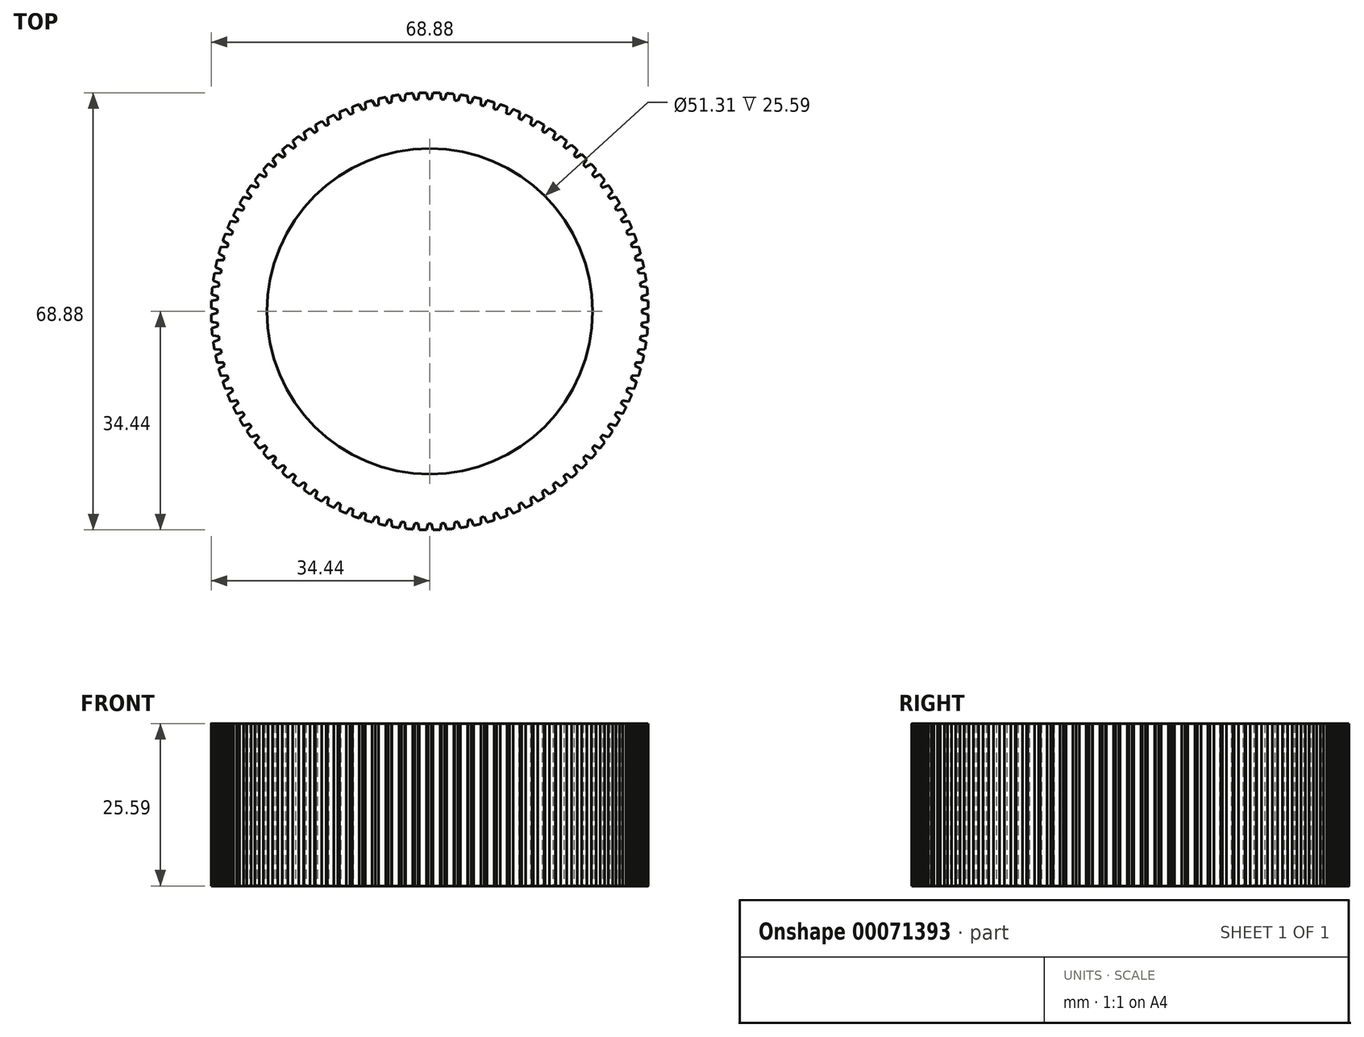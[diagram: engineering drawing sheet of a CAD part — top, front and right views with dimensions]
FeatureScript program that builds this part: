
annotation { "Feature Type Name" : "Feature", "Feature Type Description" : "" }
export const myFeature = defineFeature(function(context is Context, id is Id, definition is map)
    precondition{}
    {
        {
            var Q0;
            Q0=qCreatedBy(makeId("Top.planeOp"),FACE);
            var sketch = newSketch(context, id + "F0", { "sketchPlane" : qUnion([Q0])});
            skArc(sketch, "E0", {"start": v(-0.5, 34.44) * mm, "mid": v(-1.08, 34.43) * mm, "end": v(-1.66, 34.4) * mm});
            skCircle(sketch, "E1", {"center": v(0, 0) * mm, "radius": 25.66 * mm});
            skLineSegment(sketch, "E2", {"start": v(-0.5, 34.44) * mm, "end": v(-0.25, 33.46) * mm});
            skLineSegment(sketch, "E3", {"start": v(0.25, 33.46) * mm, "end": v(0.5, 34.44) * mm});
            skLineSegment(sketch, "E4.1.0", {"start": v(-1.85, 33.41) * mm, "end": v(-1.66, 34.4) * mm});
            skLineSegment(sketch, "E4.1.1", {"start": v(-2.66, 34.34) * mm, "end": v(-2.35, 33.38) * mm});
            skLineSegment(sketch, "E4.2.0", {"start": v(-3.95, 33.23) * mm, "end": v(-3.82, 34.23) * mm});
            skLineSegment(sketch, "E4.2.1", {"start": v(-4.81, 34.1) * mm, "end": v(-4.44, 33.17) * mm});
            skLineSegment(sketch, "E4.3.0", {"start": v(-6.02, 32.92) * mm, "end": v(-5.96, 33.93) * mm});
            skLineSegment(sketch, "E4.3.1", {"start": v(-6.94, 33.74) * mm, "end": v(-6.52, 32.82) * mm});
            skLineSegment(sketch, "E4.4.0", {"start": v(-8.08, 32.47) * mm, "end": v(-8.08, 33.48) * mm});
            skLineSegment(sketch, "E4.4.1", {"start": v(-9.05, 33.23) * mm, "end": v(-8.56, 32.35) * mm});
            skLineSegment(sketch, "E4.5.0", {"start": v(-10.1, 31.9) * mm, "end": v(-10.17, 32.91) * mm});
            skLineSegment(sketch, "E4.5.1", {"start": v(-11.12, 32.6) * mm, "end": v(-10.58, 31.75) * mm});
            skLineSegment(sketch, "E4.6.0", {"start": v(-12.09, 31.2) * mm, "end": v(-12.21, 32.2) * mm});
            skLineSegment(sketch, "E4.6.1", {"start": v(-13.14, 31.84) * mm, "end": v(-12.55, 31.02) * mm});
            skLineSegment(sketch, "E4.7.0", {"start": v(-14.02, 30.39) * mm, "end": v(-14.21, 31.38) * mm});
            skLineSegment(sketch, "E4.7.1", {"start": v(-15.12, 30.95) * mm, "end": v(-14.47, 30.17) * mm});
            skLineSegment(sketch, "E4.8.0", {"start": v(-15.9, 29.44) * mm, "end": v(-16.15, 30.42) * mm});
            skLineSegment(sketch, "E4.8.1", {"start": v(-17.03, 29.94) * mm, "end": v(-16.34, 29.2) * mm});
            skLineSegment(sketch, "E4.9.0", {"start": v(-17.72, 28.39) * mm, "end": v(-18.03, 29.35) * mm});
            skLineSegment(sketch, "E4.9.1", {"start": v(-18.88, 28.81) * mm, "end": v(-18.14, 28.12) * mm});
            skLineSegment(sketch, "E4.10.0", {"start": v(-19.47, 27.22) * mm, "end": v(-19.84, 28.16) * mm});
            skLineSegment(sketch, "E4.10.1", {"start": v(-20.65, 27.57) * mm, "end": v(-19.87, 26.93) * mm});
            skLineSegment(sketch, "E4.11.0", {"start": v(-21.14, 25.94) * mm, "end": v(-21.57, 26.86) * mm});
            skLineSegment(sketch, "E4.11.1", {"start": v(-22.34, 26.22) * mm, "end": v(-21.52, 25.62) * mm});
            skLineSegment(sketch, "E4.12.0", {"start": v(-22.73, 24.56) * mm, "end": v(-23.21, 25.45) * mm});
            skLineSegment(sketch, "E4.12.1", {"start": v(-23.94, 24.76) * mm, "end": v(-23.09, 24.22) * mm});
            skLineSegment(sketch, "E4.13.0", {"start": v(-24.22, 23.09) * mm, "end": v(-24.76, 23.94) * mm});
            skLineSegment(sketch, "E4.13.1", {"start": v(-25.45, 23.21) * mm, "end": v(-24.56, 22.73) * mm});
            skLineSegment(sketch, "E4.14.0", {"start": v(-25.62, 21.52) * mm, "end": v(-26.22, 22.34) * mm});
            skLineSegment(sketch, "E4.14.1", {"start": v(-26.86, 21.57) * mm, "end": v(-25.94, 21.14) * mm});
            skLineSegment(sketch, "E4.15.0", {"start": v(-26.93, 19.87) * mm, "end": v(-27.57, 20.65) * mm});
            skLineSegment(sketch, "E4.15.1", {"start": v(-28.16, 19.84) * mm, "end": v(-27.22, 19.47) * mm});
            skLineSegment(sketch, "E4.16.0", {"start": v(-28.12, 18.14) * mm, "end": v(-28.81, 18.88) * mm});
            skLineSegment(sketch, "E4.16.1", {"start": v(-29.35, 18.03) * mm, "end": v(-28.39, 17.72) * mm});
            skLineSegment(sketch, "E4.17.0", {"start": v(-29.2, 16.34) * mm, "end": v(-29.94, 17.03) * mm});
            skLineSegment(sketch, "E4.17.1", {"start": v(-30.42, 16.15) * mm, "end": v(-29.44, 15.9) * mm});
            skLineSegment(sketch, "E4.18.0", {"start": v(-30.17, 14.47) * mm, "end": v(-30.95, 15.12) * mm});
            skLineSegment(sketch, "E4.18.1", {"start": v(-31.38, 14.21) * mm, "end": v(-30.39, 14.02) * mm});
            skLineSegment(sketch, "E4.19.0", {"start": v(-31.02, 12.55) * mm, "end": v(-31.84, 13.14) * mm});
            skLineSegment(sketch, "E4.19.1", {"start": v(-32.2, 12.21) * mm, "end": v(-31.2, 12.09) * mm});
            skLineSegment(sketch, "E4.20.0", {"start": v(-31.75, 10.58) * mm, "end": v(-32.6, 11.12) * mm});
            skLineSegment(sketch, "E4.20.1", {"start": v(-32.91, 10.17) * mm, "end": v(-31.9, 10.1) * mm});
            skLineSegment(sketch, "E4.21.0", {"start": v(-32.35, 8.56) * mm, "end": v(-33.23, 9.05) * mm});
            skLineSegment(sketch, "E4.21.1", {"start": v(-33.48, 8.08) * mm, "end": v(-32.47, 8.08) * mm});
            skLineSegment(sketch, "E4.22.0", {"start": v(-32.82, 6.52) * mm, "end": v(-33.74, 6.94) * mm});
            skLineSegment(sketch, "E4.22.1", {"start": v(-33.93, 5.96) * mm, "end": v(-32.92, 6.02) * mm});
            skLineSegment(sketch, "E4.23.0", {"start": v(-33.17, 4.44) * mm, "end": v(-34.1, 4.81) * mm});
            skLineSegment(sketch, "E4.23.1", {"start": v(-34.23, 3.82) * mm, "end": v(-33.23, 3.95) * mm});
            skLineSegment(sketch, "E4.24.0", {"start": v(-33.38, 2.35) * mm, "end": v(-34.34, 2.66) * mm});
            skLineSegment(sketch, "E4.24.1", {"start": v(-34.4, 1.66) * mm, "end": v(-33.41, 1.85) * mm});
            skLineSegment(sketch, "E4.25.0", {"start": v(-33.46, 0.25) * mm, "end": v(-34.44, 0.5) * mm});
            skLineSegment(sketch, "E4.25.1", {"start": v(-34.44, -0.5) * mm, "end": v(-33.46, -0.25) * mm});
            skLineSegment(sketch, "E4.26.0", {"start": v(-33.41, -1.85) * mm, "end": v(-34.4, -1.66) * mm});
            skLineSegment(sketch, "E4.26.1", {"start": v(-34.34, -2.66) * mm, "end": v(-33.38, -2.35) * mm});
            skLineSegment(sketch, "E4.27.0", {"start": v(-33.23, -3.95) * mm, "end": v(-34.23, -3.82) * mm});
            skLineSegment(sketch, "E4.27.1", {"start": v(-34.1, -4.81) * mm, "end": v(-33.17, -4.44) * mm});
            skLineSegment(sketch, "E4.28.0", {"start": v(-32.92, -6.02) * mm, "end": v(-33.93, -5.96) * mm});
            skLineSegment(sketch, "E4.28.1", {"start": v(-33.74, -6.94) * mm, "end": v(-32.82, -6.52) * mm});
            skLineSegment(sketch, "E4.29.0", {"start": v(-32.47, -8.08) * mm, "end": v(-33.48, -8.08) * mm});
            skLineSegment(sketch, "E4.29.1", {"start": v(-33.23, -9.05) * mm, "end": v(-32.35, -8.56) * mm});
            skLineSegment(sketch, "E4.30.0", {"start": v(-31.9, -10.1) * mm, "end": v(-32.91, -10.17) * mm});
            skLineSegment(sketch, "E4.30.1", {"start": v(-32.6, -11.12) * mm, "end": v(-31.75, -10.58) * mm});
            skLineSegment(sketch, "E4.31.0", {"start": v(-31.2, -12.09) * mm, "end": v(-32.2, -12.21) * mm});
            skLineSegment(sketch, "E4.31.1", {"start": v(-31.84, -13.14) * mm, "end": v(-31.02, -12.55) * mm});
            skLineSegment(sketch, "E4.32.0", {"start": v(-30.39, -14.02) * mm, "end": v(-31.38, -14.21) * mm});
            skLineSegment(sketch, "E4.32.1", {"start": v(-30.95, -15.12) * mm, "end": v(-30.17, -14.47) * mm});
            skLineSegment(sketch, "E4.33.0", {"start": v(-29.44, -15.9) * mm, "end": v(-30.42, -16.15) * mm});
            skLineSegment(sketch, "E4.33.1", {"start": v(-29.94, -17.03) * mm, "end": v(-29.2, -16.34) * mm});
            skLineSegment(sketch, "E4.34.0", {"start": v(-28.39, -17.72) * mm, "end": v(-29.35, -18.03) * mm});
            skLineSegment(sketch, "E4.34.1", {"start": v(-28.81, -18.88) * mm, "end": v(-28.12, -18.14) * mm});
            skLineSegment(sketch, "E4.35.0", {"start": v(-27.22, -19.47) * mm, "end": v(-28.16, -19.84) * mm});
            skLineSegment(sketch, "E4.35.1", {"start": v(-27.57, -20.65) * mm, "end": v(-26.93, -19.87) * mm});
            skLineSegment(sketch, "E4.36.0", {"start": v(-25.94, -21.14) * mm, "end": v(-26.86, -21.57) * mm});
            skLineSegment(sketch, "E4.36.1", {"start": v(-26.22, -22.34) * mm, "end": v(-25.62, -21.52) * mm});
            skLineSegment(sketch, "E4.37.0", {"start": v(-24.56, -22.73) * mm, "end": v(-25.45, -23.21) * mm});
            skLineSegment(sketch, "E4.37.1", {"start": v(-24.76, -23.94) * mm, "end": v(-24.22, -23.09) * mm});
            skLineSegment(sketch, "E4.38.0", {"start": v(-23.09, -24.22) * mm, "end": v(-23.94, -24.76) * mm});
            skLineSegment(sketch, "E4.38.1", {"start": v(-23.21, -25.45) * mm, "end": v(-22.73, -24.56) * mm});
            skLineSegment(sketch, "E4.39.0", {"start": v(-21.52, -25.62) * mm, "end": v(-22.34, -26.22) * mm});
            skLineSegment(sketch, "E4.39.1", {"start": v(-21.57, -26.86) * mm, "end": v(-21.14, -25.94) * mm});
            skLineSegment(sketch, "E4.40.0", {"start": v(-19.87, -26.93) * mm, "end": v(-20.65, -27.57) * mm});
            skLineSegment(sketch, "E4.40.1", {"start": v(-19.84, -28.16) * mm, "end": v(-19.47, -27.22) * mm});
            skLineSegment(sketch, "E4.41.0", {"start": v(-18.14, -28.12) * mm, "end": v(-18.88, -28.81) * mm});
            skLineSegment(sketch, "E4.41.1", {"start": v(-18.03, -29.35) * mm, "end": v(-17.72, -28.39) * mm});
            skLineSegment(sketch, "E4.42.0", {"start": v(-16.34, -29.2) * mm, "end": v(-17.03, -29.94) * mm});
            skLineSegment(sketch, "E4.42.1", {"start": v(-16.15, -30.42) * mm, "end": v(-15.9, -29.44) * mm});
            skLineSegment(sketch, "E4.43.0", {"start": v(-14.47, -30.17) * mm, "end": v(-15.12, -30.95) * mm});
            skLineSegment(sketch, "E4.43.1", {"start": v(-14.21, -31.38) * mm, "end": v(-14.02, -30.39) * mm});
            skLineSegment(sketch, "E4.44.0", {"start": v(-12.55, -31.02) * mm, "end": v(-13.14, -31.84) * mm});
            skLineSegment(sketch, "E4.44.1", {"start": v(-12.21, -32.2) * mm, "end": v(-12.09, -31.2) * mm});
            skLineSegment(sketch, "E4.45.0", {"start": v(-10.58, -31.75) * mm, "end": v(-11.12, -32.6) * mm});
            skLineSegment(sketch, "E4.45.1", {"start": v(-10.17, -32.91) * mm, "end": v(-10.1, -31.9) * mm});
            skLineSegment(sketch, "E4.46.0", {"start": v(-8.56, -32.35) * mm, "end": v(-9.05, -33.23) * mm});
            skLineSegment(sketch, "E4.46.1", {"start": v(-8.08, -33.48) * mm, "end": v(-8.08, -32.47) * mm});
            skLineSegment(sketch, "E4.47.0", {"start": v(-6.52, -32.82) * mm, "end": v(-6.94, -33.74) * mm});
            skLineSegment(sketch, "E4.47.1", {"start": v(-5.96, -33.93) * mm, "end": v(-6.02, -32.92) * mm});
            skLineSegment(sketch, "E4.48.0", {"start": v(-4.44, -33.17) * mm, "end": v(-4.81, -34.1) * mm});
            skLineSegment(sketch, "E4.48.1", {"start": v(-3.82, -34.23) * mm, "end": v(-3.95, -33.23) * mm});
            skLineSegment(sketch, "E4.49.0", {"start": v(-2.35, -33.38) * mm, "end": v(-2.66, -34.34) * mm});
            skLineSegment(sketch, "E4.49.1", {"start": v(-1.66, -34.4) * mm, "end": v(-1.85, -33.41) * mm});
            skLineSegment(sketch, "E4.50.0", {"start": v(-0.25, -33.46) * mm, "end": v(-0.5, -34.44) * mm});
            skLineSegment(sketch, "E4.50.1", {"start": v(0.5, -34.44) * mm, "end": v(0.25, -33.46) * mm});
            skLineSegment(sketch, "E4.51.0", {"start": v(1.85, -33.41) * mm, "end": v(1.66, -34.4) * mm});
            skLineSegment(sketch, "E4.51.1", {"start": v(2.66, -34.34) * mm, "end": v(2.35, -33.38) * mm});
            skLineSegment(sketch, "E4.52.0", {"start": v(3.95, -33.23) * mm, "end": v(3.82, -34.23) * mm});
            skLineSegment(sketch, "E4.52.1", {"start": v(4.81, -34.1) * mm, "end": v(4.44, -33.17) * mm});
            skLineSegment(sketch, "E4.53.0", {"start": v(6.02, -32.92) * mm, "end": v(5.96, -33.93) * mm});
            skLineSegment(sketch, "E4.53.1", {"start": v(6.94, -33.74) * mm, "end": v(6.52, -32.82) * mm});
            skLineSegment(sketch, "E4.54.0", {"start": v(8.08, -32.47) * mm, "end": v(8.08, -33.48) * mm});
            skLineSegment(sketch, "E4.54.1", {"start": v(9.05, -33.23) * mm, "end": v(8.56, -32.35) * mm});
            skLineSegment(sketch, "E4.55.0", {"start": v(10.1, -31.9) * mm, "end": v(10.17, -32.91) * mm});
            skLineSegment(sketch, "E4.55.1", {"start": v(11.12, -32.6) * mm, "end": v(10.58, -31.75) * mm});
            skLineSegment(sketch, "E4.56.0", {"start": v(12.09, -31.2) * mm, "end": v(12.21, -32.2) * mm});
            skLineSegment(sketch, "E4.56.1", {"start": v(13.14, -31.84) * mm, "end": v(12.55, -31.02) * mm});
            skLineSegment(sketch, "E4.57.0", {"start": v(14.02, -30.39) * mm, "end": v(14.21, -31.38) * mm});
            skLineSegment(sketch, "E4.57.1", {"start": v(15.12, -30.95) * mm, "end": v(14.47, -30.17) * mm});
            skLineSegment(sketch, "E4.58.0", {"start": v(15.9, -29.44) * mm, "end": v(16.15, -30.42) * mm});
            skLineSegment(sketch, "E4.58.1", {"start": v(17.03, -29.94) * mm, "end": v(16.34, -29.2) * mm});
            skLineSegment(sketch, "E4.59.0", {"start": v(17.72, -28.39) * mm, "end": v(18.03, -29.35) * mm});
            skLineSegment(sketch, "E4.59.1", {"start": v(18.88, -28.81) * mm, "end": v(18.14, -28.12) * mm});
            skLineSegment(sketch, "E4.60.0", {"start": v(19.47, -27.22) * mm, "end": v(19.84, -28.16) * mm});
            skLineSegment(sketch, "E4.60.1", {"start": v(20.65, -27.57) * mm, "end": v(19.87, -26.93) * mm});
            skLineSegment(sketch, "E4.61.0", {"start": v(21.14, -25.94) * mm, "end": v(21.57, -26.86) * mm});
            skLineSegment(sketch, "E4.61.1", {"start": v(22.34, -26.22) * mm, "end": v(21.52, -25.62) * mm});
            skLineSegment(sketch, "E4.62.0", {"start": v(22.73, -24.56) * mm, "end": v(23.21, -25.45) * mm});
            skLineSegment(sketch, "E4.62.1", {"start": v(23.94, -24.76) * mm, "end": v(23.09, -24.22) * mm});
            skLineSegment(sketch, "E4.63.0", {"start": v(24.22, -23.09) * mm, "end": v(24.76, -23.94) * mm});
            skLineSegment(sketch, "E4.63.1", {"start": v(25.45, -23.21) * mm, "end": v(24.56, -22.73) * mm});
            skLineSegment(sketch, "E4.64.0", {"start": v(25.62, -21.52) * mm, "end": v(26.22, -22.34) * mm});
            skLineSegment(sketch, "E4.64.1", {"start": v(26.86, -21.57) * mm, "end": v(25.94, -21.14) * mm});
            skLineSegment(sketch, "E4.65.0", {"start": v(26.93, -19.87) * mm, "end": v(27.57, -20.65) * mm});
            skLineSegment(sketch, "E4.65.1", {"start": v(28.16, -19.84) * mm, "end": v(27.22, -19.47) * mm});
            skLineSegment(sketch, "E4.66.0", {"start": v(28.12, -18.14) * mm, "end": v(28.81, -18.88) * mm});
            skLineSegment(sketch, "E4.66.1", {"start": v(29.35, -18.03) * mm, "end": v(28.39, -17.72) * mm});
            skLineSegment(sketch, "E4.67.0", {"start": v(29.2, -16.34) * mm, "end": v(29.94, -17.03) * mm});
            skLineSegment(sketch, "E4.67.1", {"start": v(30.42, -16.15) * mm, "end": v(29.44, -15.9) * mm});
            skLineSegment(sketch, "E4.68.0", {"start": v(30.17, -14.47) * mm, "end": v(30.95, -15.12) * mm});
            skLineSegment(sketch, "E4.68.1", {"start": v(31.38, -14.21) * mm, "end": v(30.39, -14.02) * mm});
            skLineSegment(sketch, "E4.69.0", {"start": v(31.02, -12.55) * mm, "end": v(31.84, -13.14) * mm});
            skLineSegment(sketch, "E4.69.1", {"start": v(32.2, -12.21) * mm, "end": v(31.2, -12.09) * mm});
            skLineSegment(sketch, "E4.70.0", {"start": v(31.75, -10.58) * mm, "end": v(32.6, -11.12) * mm});
            skLineSegment(sketch, "E4.70.1", {"start": v(32.91, -10.17) * mm, "end": v(31.9, -10.1) * mm});
            skLineSegment(sketch, "E4.71.0", {"start": v(32.35, -8.56) * mm, "end": v(33.23, -9.05) * mm});
            skLineSegment(sketch, "E4.71.1", {"start": v(33.48, -8.08) * mm, "end": v(32.47, -8.08) * mm});
            skLineSegment(sketch, "E4.72.0", {"start": v(32.82, -6.52) * mm, "end": v(33.74, -6.94) * mm});
            skLineSegment(sketch, "E4.72.1", {"start": v(33.93, -5.96) * mm, "end": v(32.92, -6.02) * mm});
            skLineSegment(sketch, "E4.73.0", {"start": v(33.17, -4.44) * mm, "end": v(34.1, -4.81) * mm});
            skLineSegment(sketch, "E4.73.1", {"start": v(34.23, -3.82) * mm, "end": v(33.23, -3.95) * mm});
            skLineSegment(sketch, "E4.74.0", {"start": v(33.38, -2.35) * mm, "end": v(34.34, -2.66) * mm});
            skLineSegment(sketch, "E4.74.1", {"start": v(34.4, -1.66) * mm, "end": v(33.41, -1.85) * mm});
            skLineSegment(sketch, "E4.75.0", {"start": v(33.46, -0.25) * mm, "end": v(34.44, -0.5) * mm});
            skLineSegment(sketch, "E4.75.1", {"start": v(34.44, 0.5) * mm, "end": v(33.46, 0.25) * mm});
            skLineSegment(sketch, "E4.76.0", {"start": v(33.41, 1.85) * mm, "end": v(34.4, 1.66) * mm});
            skLineSegment(sketch, "E4.76.1", {"start": v(34.34, 2.66) * mm, "end": v(33.38, 2.35) * mm});
            skLineSegment(sketch, "E4.77.0", {"start": v(33.23, 3.95) * mm, "end": v(34.23, 3.82) * mm});
            skLineSegment(sketch, "E4.77.1", {"start": v(34.1, 4.81) * mm, "end": v(33.17, 4.44) * mm});
            skLineSegment(sketch, "E4.78.0", {"start": v(32.92, 6.02) * mm, "end": v(33.93, 5.96) * mm});
            skLineSegment(sketch, "E4.78.1", {"start": v(33.74, 6.94) * mm, "end": v(32.82, 6.52) * mm});
            skLineSegment(sketch, "E4.79.0", {"start": v(32.47, 8.08) * mm, "end": v(33.48, 8.08) * mm});
            skLineSegment(sketch, "E4.79.1", {"start": v(33.23, 9.05) * mm, "end": v(32.35, 8.56) * mm});
            skLineSegment(sketch, "E4.80.0", {"start": v(31.9, 10.1) * mm, "end": v(32.91, 10.17) * mm});
            skLineSegment(sketch, "E4.80.1", {"start": v(32.6, 11.12) * mm, "end": v(31.75, 10.58) * mm});
            skLineSegment(sketch, "E4.81.0", {"start": v(31.2, 12.09) * mm, "end": v(32.2, 12.21) * mm});
            skLineSegment(sketch, "E4.81.1", {"start": v(31.84, 13.14) * mm, "end": v(31.02, 12.55) * mm});
            skLineSegment(sketch, "E4.82.0", {"start": v(30.39, 14.02) * mm, "end": v(31.38, 14.21) * mm});
            skLineSegment(sketch, "E4.82.1", {"start": v(30.95, 15.12) * mm, "end": v(30.17, 14.47) * mm});
            skLineSegment(sketch, "E4.83.0", {"start": v(29.44, 15.9) * mm, "end": v(30.42, 16.15) * mm});
            skLineSegment(sketch, "E4.83.1", {"start": v(29.94, 17.03) * mm, "end": v(29.2, 16.34) * mm});
            skLineSegment(sketch, "E4.84.0", {"start": v(28.39, 17.72) * mm, "end": v(29.35, 18.03) * mm});
            skLineSegment(sketch, "E4.84.1", {"start": v(28.81, 18.88) * mm, "end": v(28.12, 18.14) * mm});
            skLineSegment(sketch, "E4.85.0", {"start": v(27.22, 19.47) * mm, "end": v(28.16, 19.84) * mm});
            skLineSegment(sketch, "E4.85.1", {"start": v(27.57, 20.65) * mm, "end": v(26.93, 19.87) * mm});
            skLineSegment(sketch, "E4.86.0", {"start": v(25.94, 21.14) * mm, "end": v(26.86, 21.57) * mm});
            skLineSegment(sketch, "E4.86.1", {"start": v(26.22, 22.34) * mm, "end": v(25.62, 21.52) * mm});
            skLineSegment(sketch, "E4.87.0", {"start": v(24.56, 22.73) * mm, "end": v(25.45, 23.21) * mm});
            skLineSegment(sketch, "E4.87.1", {"start": v(24.76, 23.94) * mm, "end": v(24.22, 23.09) * mm});
            skLineSegment(sketch, "E4.88.0", {"start": v(23.09, 24.22) * mm, "end": v(23.94, 24.76) * mm});
            skLineSegment(sketch, "E4.88.1", {"start": v(23.21, 25.45) * mm, "end": v(22.73, 24.56) * mm});
            skLineSegment(sketch, "E4.89.0", {"start": v(21.52, 25.62) * mm, "end": v(22.34, 26.22) * mm});
            skLineSegment(sketch, "E4.89.1", {"start": v(21.57, 26.86) * mm, "end": v(21.14, 25.94) * mm});
            skLineSegment(sketch, "E4.90.0", {"start": v(19.87, 26.93) * mm, "end": v(20.65, 27.57) * mm});
            skLineSegment(sketch, "E4.90.1", {"start": v(19.84, 28.16) * mm, "end": v(19.47, 27.22) * mm});
            skLineSegment(sketch, "E4.91.0", {"start": v(18.14, 28.12) * mm, "end": v(18.88, 28.81) * mm});
            skLineSegment(sketch, "E4.91.1", {"start": v(18.03, 29.35) * mm, "end": v(17.72, 28.39) * mm});
            skLineSegment(sketch, "E4.92.0", {"start": v(16.34, 29.2) * mm, "end": v(17.03, 29.94) * mm});
            skLineSegment(sketch, "E4.92.1", {"start": v(16.15, 30.42) * mm, "end": v(15.9, 29.44) * mm});
            skLineSegment(sketch, "E4.93.0", {"start": v(14.47, 30.17) * mm, "end": v(15.12, 30.95) * mm});
            skLineSegment(sketch, "E4.93.1", {"start": v(14.21, 31.38) * mm, "end": v(14.02, 30.39) * mm});
            skLineSegment(sketch, "E4.94.0", {"start": v(12.55, 31.02) * mm, "end": v(13.14, 31.84) * mm});
            skLineSegment(sketch, "E4.94.1", {"start": v(12.21, 32.2) * mm, "end": v(12.09, 31.2) * mm});
            skLineSegment(sketch, "E4.95.0", {"start": v(10.58, 31.75) * mm, "end": v(11.12, 32.6) * mm});
            skLineSegment(sketch, "E4.95.1", {"start": v(10.17, 32.91) * mm, "end": v(10.1, 31.9) * mm});
            skLineSegment(sketch, "E4.96.0", {"start": v(8.56, 32.35) * mm, "end": v(9.05, 33.23) * mm});
            skLineSegment(sketch, "E4.96.1", {"start": v(8.08, 33.48) * mm, "end": v(8.08, 32.47) * mm});
            skLineSegment(sketch, "E4.97.0", {"start": v(6.52, 32.82) * mm, "end": v(6.94, 33.74) * mm});
            skLineSegment(sketch, "E4.97.1", {"start": v(5.96, 33.93) * mm, "end": v(6.02, 32.92) * mm});
            skLineSegment(sketch, "E4.98.0", {"start": v(4.44, 33.17) * mm, "end": v(4.81, 34.1) * mm});
            skLineSegment(sketch, "E4.98.1", {"start": v(3.82, 34.23) * mm, "end": v(3.95, 33.23) * mm});
            skLineSegment(sketch, "E4.99.0", {"start": v(2.35, 33.38) * mm, "end": v(2.66, 34.34) * mm});
            skLineSegment(sketch, "E4.99.1", {"start": v(1.66, 34.4) * mm, "end": v(1.85, 33.41) * mm});
            skArc(sketch, "E5.trimOffspring", {"start": v(1.66, 34.4) * mm, "mid": v(1.08, 34.43) * mm, "end": v(0.5, 34.44) * mm});
            skArc(sketch, "E6.trimOffspring", {"start": v(3.82, 34.23) * mm, "mid": v(3.24, 34.3) * mm, "end": v(2.66, 34.34) * mm});
            skArc(sketch, "E7.trimOffspring", {"start": v(5.96, 33.93) * mm, "mid": v(5.39, 34.02) * mm, "end": v(4.81, 34.1) * mm});
            skArc(sketch, "E8.trimOffspring", {"start": v(8.08, 33.48) * mm, "mid": v(7.51, 33.62) * mm, "end": v(6.94, 33.74) * mm});
            skArc(sketch, "E9.trimOffspring", {"start": v(10.17, 32.91) * mm, "mid": v(9.6, 33.08) * mm, "end": v(9.05, 33.23) * mm});
            skArc(sketch, "E10.trimOffspring", {"start": v(12.21, 32.2) * mm, "mid": v(11.67, 32.4) * mm, "end": v(11.12, 32.6) * mm});
            skArc(sketch, "E11.trimOffspring", {"start": v(14.21, 31.38) * mm, "mid": v(13.68, 31.61) * mm, "end": v(13.14, 31.84) * mm});
            skArc(sketch, "E12.trimOffspring", {"start": v(16.15, 30.42) * mm, "mid": v(15.64, 30.7) * mm, "end": v(15.12, 30.95) * mm});
            skArc(sketch, "E13.trimOffspring", {"start": v(18.03, 29.35) * mm, "mid": v(17.53, 29.65) * mm, "end": v(17.03, 29.94) * mm});
            skArc(sketch, "E14.trimOffspring", {"start": v(19.84, 28.16) * mm, "mid": v(19.36, 28.49) * mm, "end": v(18.88, 28.81) * mm});
            skArc(sketch, "E15.trimOffspring", {"start": v(21.57, 26.86) * mm, "mid": v(21.11, 27.22) * mm, "end": v(20.65, 27.57) * mm});
            skArc(sketch, "E16.trimOffspring", {"start": v(23.21, 25.45) * mm, "mid": v(22.78, 25.84) * mm, "end": v(22.34, 26.22) * mm});
            skArc(sketch, "E17.trimOffspring", {"start": v(24.76, 23.94) * mm, "mid": v(24.36, 24.36) * mm, "end": v(23.94, 24.76) * mm});
            skArc(sketch, "E18.trimOffspring", {"start": v(26.22, 22.34) * mm, "mid": v(25.84, 22.78) * mm, "end": v(25.45, 23.21) * mm});
            skArc(sketch, "E19.trimOffspring", {"start": v(27.57, 20.65) * mm, "mid": v(27.22, 21.11) * mm, "end": v(26.86, 21.57) * mm});
            skArc(sketch, "E20.trimOffspring", {"start": v(28.81, 18.88) * mm, "mid": v(28.49, 19.36) * mm, "end": v(28.16, 19.84) * mm});
            skArc(sketch, "E21.trimOffspring", {"start": v(29.94, 17.03) * mm, "mid": v(29.65, 17.53) * mm, "end": v(29.35, 18.03) * mm});
            skArc(sketch, "E22.trimOffspring", {"start": v(30.95, 15.12) * mm, "mid": v(30.7, 15.64) * mm, "end": v(30.42, 16.15) * mm});
            skArc(sketch, "E23.trimOffspring", {"start": v(30.39, 14.02) * mm, "mid": v(30.28, 14.25) * mm, "end": v(30.17, 14.47) * mm});
            skArc(sketch, "E24.trimOffspring", {"start": v(31.84, 13.14) * mm, "mid": v(31.61, 13.68) * mm, "end": v(31.38, 14.21) * mm});
            skArc(sketch, "E25.trimOffspring", {"start": v(31.2, 12.09) * mm, "mid": v(31.11, 12.32) * mm, "end": v(31.02, 12.55) * mm});
            skArc(sketch, "E26.trimOffspring", {"start": v(32.6, 11.12) * mm, "mid": v(32.4, 11.67) * mm, "end": v(32.2, 12.21) * mm});
            skArc(sketch, "E27.trimOffspring", {"start": v(31.9, 10.1) * mm, "mid": v(31.83, 10.34) * mm, "end": v(31.75, 10.58) * mm});
            skArc(sketch, "E28.trimOffspring", {"start": v(33.23, 9.05) * mm, "mid": v(33.08, 9.6) * mm, "end": v(32.91, 10.17) * mm});
            skArc(sketch, "E29.trimOffspring", {"start": v(32.47, 8.08) * mm, "mid": v(32.41, 8.32) * mm, "end": v(32.35, 8.56) * mm});
            skArc(sketch, "E30.trimOffspring", {"start": v(33.74, 6.94) * mm, "mid": v(33.62, 7.51) * mm, "end": v(33.48, 8.08) * mm});
            skArc(sketch, "E31.trimOffspring", {"start": v(32.92, 6.02) * mm, "mid": v(32.87, 6.27) * mm, "end": v(32.82, 6.52) * mm});
            skArc(sketch, "E32.trimOffspring", {"start": v(34.1, 4.81) * mm, "mid": v(34.02, 5.39) * mm, "end": v(33.93, 5.96) * mm});
            skArc(sketch, "E33.trimOffspring", {"start": v(33.23, 3.95) * mm, "mid": v(33.2, 4.2) * mm, "end": v(33.17, 4.44) * mm});
            skArc(sketch, "E34.trimOffspring", {"start": v(34.34, 2.66) * mm, "mid": v(34.3, 3.24) * mm, "end": v(34.23, 3.82) * mm});
            skArc(sketch, "E35.trimOffspring", {"start": v(33.41, 1.85) * mm, "mid": v(33.4, 2.1) * mm, "end": v(33.38, 2.35) * mm});
            skArc(sketch, "E36.trimOffspring", {"start": v(34.44, 0.5) * mm, "mid": v(34.43, 1.08) * mm, "end": v(34.4, 1.66) * mm});
            skArc(sketch, "E37.trimOffspring", {"start": v(33.46, -0.25) * mm, "mid": v(33.46, 0) * mm, "end": v(33.46, 0.25) * mm});
            skArc(sketch, "E38.trimOffspring", {"start": v(28.39, 17.72) * mm, "mid": v(28.25, 17.93) * mm, "end": v(28.12, 18.14) * mm});
            skArc(sketch, "E39.trimOffspring", {"start": v(24.56, 22.73) * mm, "mid": v(24.4, 22.9) * mm, "end": v(24.22, 23.09) * mm});
            skArc(sketch, "E40.trimOffspring", {"start": v(23.09, 24.22) * mm, "mid": v(22.9, 24.4) * mm, "end": v(22.73, 24.56) * mm});
            skArc(sketch, "E41.trimOffspring", {"start": v(25.94, 21.14) * mm, "mid": v(25.78, 21.33) * mm, "end": v(25.62, 21.52) * mm});
            skArc(sketch, "E42.trimOffspring", {"start": v(27.22, 19.47) * mm, "mid": v(27.07, 19.67) * mm, "end": v(26.93, 19.87) * mm});
            skArc(sketch, "E43.trimOffspring", {"start": v(21.52, 25.62) * mm, "mid": v(21.33, 25.78) * mm, "end": v(21.14, 25.94) * mm});
            skArc(sketch, "E44.trimOffspring", {"start": v(16.34, 29.2) * mm, "mid": v(16.12, 29.33) * mm, "end": v(15.9, 29.44) * mm});
            skArc(sketch, "E45.trimOffspring", {"start": v(14.47, 30.17) * mm, "mid": v(14.25, 30.28) * mm, "end": v(14.02, 30.39) * mm});
            skArc(sketch, "E46.trimOffspring", {"start": v(10.58, 31.75) * mm, "mid": v(10.34, 31.83) * mm, "end": v(10.1, 31.9) * mm});
            skArc(sketch, "E47.trimOffspring", {"start": v(4.44, 33.17) * mm, "mid": v(4.2, 33.2) * mm, "end": v(3.95, 33.23) * mm});
            skArc(sketch, "E48.trimOffspring", {"start": v(6.52, 32.82) * mm, "mid": v(6.27, 32.87) * mm, "end": v(6.02, 32.92) * mm});
            skArc(sketch, "E49.trimOffspring", {"start": v(8.56, 32.35) * mm, "mid": v(8.32, 32.41) * mm, "end": v(8.08, 32.47) * mm});
            skArc(sketch, "E50.trimOffspring", {"start": v(2.35, 33.38) * mm, "mid": v(2.1, 33.4) * mm, "end": v(1.85, 33.41) * mm});
            skArc(sketch, "E51.trimOffspring", {"start": v(0.25, 33.46) * mm, "mid": v(0, 33.46) * mm, "end": v(-0.25, 33.46) * mm});
            skArc(sketch, "E52.trimOffspring", {"start": v(-1.85, 33.41) * mm, "mid": v(-2.1, 33.4) * mm, "end": v(-2.35, 33.38) * mm});
            skArc(sketch, "E53.trimOffspring", {"start": v(-2.66, 34.34) * mm, "mid": v(-3.24, 34.3) * mm, "end": v(-3.82, 34.23) * mm});
            skArc(sketch, "E54.trimOffspring", {"start": v(-3.95, 33.23) * mm, "mid": v(-4.2, 33.2) * mm, "end": v(-4.44, 33.17) * mm});
            skArc(sketch, "E55.trimOffspring", {"start": v(-4.81, 34.1) * mm, "mid": v(-5.39, 34.02) * mm, "end": v(-5.96, 33.93) * mm});
            skArc(sketch, "E56.trimOffspring", {"start": v(-6.02, 32.92) * mm, "mid": v(-6.27, 32.87) * mm, "end": v(-6.52, 32.82) * mm});
            skArc(sketch, "E57.trimOffspring", {"start": v(-6.94, 33.74) * mm, "mid": v(-7.51, 33.62) * mm, "end": v(-8.08, 33.48) * mm});
            skArc(sketch, "E58.trimOffspring", {"start": v(-9.05, 33.23) * mm, "mid": v(-9.6, 33.08) * mm, "end": v(-10.17, 32.91) * mm});
            skArc(sketch, "E59.trimOffspring", {"start": v(-10.1, 31.9) * mm, "mid": v(-10.34, 31.83) * mm, "end": v(-10.58, 31.75) * mm});
            skArc(sketch, "E60.trimOffspring", {"start": v(-14.02, 30.39) * mm, "mid": v(-14.25, 30.28) * mm, "end": v(-14.47, 30.17) * mm});
            skArc(sketch, "E61.trimOffspring", {"start": v(-15.12, 30.95) * mm, "mid": v(-15.64, 30.7) * mm, "end": v(-16.15, 30.42) * mm});
            skArc(sketch, "E62.trimOffspring", {"start": v(-15.9, 29.44) * mm, "mid": v(-16.12, 29.33) * mm, "end": v(-16.34, 29.2) * mm});
            skArc(sketch, "E63.trimOffspring", {"start": v(-17.03, 29.94) * mm, "mid": v(-17.53, 29.65) * mm, "end": v(-18.03, 29.35) * mm});
            skArc(sketch, "E64.trimOffspring", {"start": v(-11.12, 32.6) * mm, "mid": v(-11.67, 32.4) * mm, "end": v(-12.21, 32.2) * mm});
            skArc(sketch, "E65.trimOffspring", {"start": v(-12.09, 31.2) * mm, "mid": v(-12.32, 31.11) * mm, "end": v(-12.55, 31.02) * mm});
            skArc(sketch, "E66.trimOffspring", {"start": v(-13.14, 31.84) * mm, "mid": v(-13.68, 31.61) * mm, "end": v(-14.21, 31.38) * mm});
            skArc(sketch, "E67.trimOffspring", {"start": v(-17.72, 28.39) * mm, "mid": v(-17.93, 28.25) * mm, "end": v(-18.14, 28.12) * mm});
            skArc(sketch, "E68.trimOffspring", {"start": v(-18.88, 28.81) * mm, "mid": v(-19.36, 28.49) * mm, "end": v(-19.84, 28.16) * mm});
            skArc(sketch, "E69.trimOffspring", {"start": v(-19.47, 27.22) * mm, "mid": v(-19.67, 27.07) * mm, "end": v(-19.87, 26.93) * mm});
            skArc(sketch, "E70.trimOffspring", {"start": v(-20.65, 27.57) * mm, "mid": v(-21.11, 27.22) * mm, "end": v(-21.57, 26.86) * mm});
            skArc(sketch, "E71.trimOffspring", {"start": v(-21.14, 25.94) * mm, "mid": v(-21.33, 25.78) * mm, "end": v(-21.52, 25.62) * mm});
            skArc(sketch, "E72.trimOffspring", {"start": v(-22.34, 26.22) * mm, "mid": v(-22.78, 25.84) * mm, "end": v(-23.21, 25.45) * mm});
            skArc(sketch, "E73.trimOffspring", {"start": v(-22.73, 24.56) * mm, "mid": v(-22.9, 24.4) * mm, "end": v(-23.09, 24.22) * mm});
            skArc(sketch, "E74.trimOffspring", {"start": v(-23.94, 24.76) * mm, "mid": v(-24.36, 24.36) * mm, "end": v(-24.76, 23.94) * mm});
            skArc(sketch, "E75.trimOffspring", {"start": v(-24.22, 23.09) * mm, "mid": v(-24.4, 22.9) * mm, "end": v(-24.56, 22.73) * mm});
            skArc(sketch, "E76.trimOffspring", {"start": v(-25.45, 23.21) * mm, "mid": v(-25.84, 22.78) * mm, "end": v(-26.22, 22.34) * mm});
            skArc(sketch, "E77.trimOffspring", {"start": v(-28.16, 19.84) * mm, "mid": v(-28.49, 19.36) * mm, "end": v(-28.81, 18.88) * mm});
            skLineSegment(sketch, "E78", {"start": v(-25.62, 21.52) * mm, "end": v(-25.94, 21.14) * mm});
            skLineSegment(sketch, "E79", {"start": v(-27.57, 20.65) * mm, "end": v(-26.86, 21.57) * mm});
            skArc(sketch, "E80.trimOffspring", {"start": v(-28.12, 18.14) * mm, "mid": v(-28.25, 17.93) * mm, "end": v(-28.39, 17.72) * mm});
            skArc(sketch, "E81.trimOffspring", {"start": v(-29.35, 18.03) * mm, "mid": v(-29.65, 17.53) * mm, "end": v(-29.94, 17.03) * mm});
            skArc(sketch, "E82.trimOffspring", {"start": v(-30.42, 16.15) * mm, "mid": v(-30.7, 15.64) * mm, "end": v(-30.95, 15.12) * mm});
            skArc(sketch, "E83.trimOffspring", {"start": v(-29.2, 16.34) * mm, "mid": v(-29.33, 16.12) * mm, "end": v(-29.44, 15.9) * mm});
            skArc(sketch, "E84.trimOffspring", {"start": v(-31.38, 14.21) * mm, "mid": v(-31.61, 13.68) * mm, "end": v(-31.84, 13.14) * mm});
            skArc(sketch, "E85.trimOffspring", {"start": v(-31.02, 12.55) * mm, "mid": v(-31.11, 12.32) * mm, "end": v(-31.2, 12.09) * mm});
            skArc(sketch, "E86.trimOffspring", {"start": v(-32.2, 12.21) * mm, "mid": v(-32.4, 11.67) * mm, "end": v(-32.6, 11.12) * mm});
            skArc(sketch, "E87.trimOffspring", {"start": v(-32.91, 10.17) * mm, "mid": v(-33.08, 9.6) * mm, "end": v(-33.23, 9.05) * mm});
            skArc(sketch, "E88.trimOffspring", {"start": v(-31.75, 10.58) * mm, "mid": v(-31.83, 10.34) * mm, "end": v(-31.9, 10.1) * mm});
            skLineSegment(sketch, "E89", {"start": v(-30.17, 14.47) * mm, "end": v(-30.39, 14.02) * mm});
            skArc(sketch, "E90.trimOffspring", {"start": v(-32.35, 8.56) * mm, "mid": v(-32.41, 8.32) * mm, "end": v(-32.47, 8.08) * mm});
            skArc(sketch, "E91.trimOffspring", {"start": v(-33.48, 8.08) * mm, "mid": v(-33.62, 7.51) * mm, "end": v(-33.74, 6.94) * mm});
            skArc(sketch, "E92.trimOffspring", {"start": v(-32.82, 6.52) * mm, "mid": v(-32.87, 6.27) * mm, "end": v(-32.92, 6.02) * mm});
            skArc(sketch, "E93.trimOffspring", {"start": v(-33.93, 5.96) * mm, "mid": v(-34.02, 5.39) * mm, "end": v(-34.1, 4.81) * mm});
            skArc(sketch, "E94.trimOffspring", {"start": v(-33.17, 4.44) * mm, "mid": v(-33.2, 4.2) * mm, "end": v(-33.23, 3.95) * mm});
            skArc(sketch, "E95.trimOffspring", {"start": v(-34.23, 3.82) * mm, "mid": v(-34.3, 3.24) * mm, "end": v(-34.34, 2.66) * mm});
            skArc(sketch, "E96.trimOffspring", {"start": v(-33.38, 2.35) * mm, "mid": v(-33.4, 2.1) * mm, "end": v(-33.41, 1.85) * mm});
            skArc(sketch, "E97.trimOffspring", {"start": v(-34.4, 1.66) * mm, "mid": v(-34.43, 1.08) * mm, "end": v(-34.44, 0.5) * mm});
            skArc(sketch, "E98.trimOffspring", {"start": v(-33.46, 0.25) * mm, "mid": v(-33.46, 0) * mm, "end": v(-33.46, -0.25) * mm});
            skArc(sketch, "E99.trimOffspring", {"start": v(-34.44, -0.5) * mm, "mid": v(-34.43, -1.08) * mm, "end": v(-34.4, -1.66) * mm});
            skArc(sketch, "E100.trimOffspring", {"start": v(-33.41, -1.85) * mm, "mid": v(-33.4, -2.1) * mm, "end": v(-33.38, -2.35) * mm});
            skLineSegment(sketch, "E101", {"start": v(-26.93, 19.87) * mm, "end": v(-27.22, 19.47) * mm});
            skArc(sketch, "E102.trimOffspring", {"start": v(-34.34, -2.66) * mm, "mid": v(-34.3, -3.24) * mm, "end": v(-34.23, -3.82) * mm});
            skArc(sketch, "E103.trimOffspring", {"start": v(-33.23, -3.95) * mm, "mid": v(-33.2, -4.2) * mm, "end": v(-33.17, -4.44) * mm});
            skArc(sketch, "E104.trimOffspring", {"start": v(-34.1, -4.81) * mm, "mid": v(-34.02, -5.39) * mm, "end": v(-33.93, -5.96) * mm});
            skArc(sketch, "E105.trimOffspring", {"start": v(-32.92, -6.02) * mm, "mid": v(-32.87, -6.27) * mm, "end": v(-32.82, -6.52) * mm});
            skArc(sketch, "E106.trimOffspring", {"start": v(-33.74, -6.94) * mm, "mid": v(-33.62, -7.51) * mm, "end": v(-33.48, -8.08) * mm});
            skArc(sketch, "E107.trimOffspring", {"start": v(-32.47, -8.08) * mm, "mid": v(-32.41, -8.32) * mm, "end": v(-32.35, -8.56) * mm});
            skArc(sketch, "E108.trimOffspring", {"start": v(-33.23, -9.05) * mm, "mid": v(-33.08, -9.6) * mm, "end": v(-32.91, -10.17) * mm});
            skArc(sketch, "E109.trimOffspring", {"start": v(-31.9, -10.1) * mm, "mid": v(-31.83, -10.34) * mm, "end": v(-31.75, -10.58) * mm});
            skArc(sketch, "E110.trimOffspring", {"start": v(-32.6, -11.12) * mm, "mid": v(-32.4, -11.67) * mm, "end": v(-32.2, -12.21) * mm});
            skArc(sketch, "E111.trimOffspring", {"start": v(-31.2, -12.09) * mm, "mid": v(-31.11, -12.32) * mm, "end": v(-31.02, -12.55) * mm});
            skArc(sketch, "E112.trimOffspring", {"start": v(-31.84, -13.14) * mm, "mid": v(-31.61, -13.68) * mm, "end": v(-31.38, -14.21) * mm});
            skArc(sketch, "E113.trimOffspring", {"start": v(-30.39, -14.02) * mm, "mid": v(-30.28, -14.25) * mm, "end": v(-30.17, -14.47) * mm});
            skArc(sketch, "E114.trimOffspring", {"start": v(-30.95, -15.12) * mm, "mid": v(-30.7, -15.64) * mm, "end": v(-30.42, -16.15) * mm});
            skArc(sketch, "E115.trimOffspring", {"start": v(-29.44, -15.9) * mm, "mid": v(-29.33, -16.12) * mm, "end": v(-29.2, -16.34) * mm});
            skArc(sketch, "E116.trimOffspring", {"start": v(-29.94, -17.03) * mm, "mid": v(-29.65, -17.53) * mm, "end": v(-29.35, -18.03) * mm});
            skArc(sketch, "E117.trimOffspring", {"start": v(-28.39, -17.72) * mm, "mid": v(-28.25, -17.93) * mm, "end": v(-28.12, -18.14) * mm});
            skArc(sketch, "E118.trimOffspring", {"start": v(-28.81, -18.88) * mm, "mid": v(-28.49, -19.36) * mm, "end": v(-28.16, -19.84) * mm});
            skArc(sketch, "E119.trimOffspring", {"start": v(-27.22, -19.47) * mm, "mid": v(-27.07, -19.67) * mm, "end": v(-26.93, -19.87) * mm});
            skArc(sketch, "E120.trimOffspring", {"start": v(-27.57, -20.65) * mm, "mid": v(-27.22, -21.11) * mm, "end": v(-26.86, -21.57) * mm});
            skArc(sketch, "E121.trimOffspring", {"start": v(-25.94, -21.14) * mm, "mid": v(-25.78, -21.33) * mm, "end": v(-25.62, -21.52) * mm});
            skArc(sketch, "E122.trimOffspring", {"start": v(-26.22, -22.34) * mm, "mid": v(-25.84, -22.78) * mm, "end": v(-25.45, -23.21) * mm});
            skArc(sketch, "E123.trimOffspring", {"start": v(-24.56, -22.73) * mm, "mid": v(-24.4, -22.9) * mm, "end": v(-24.22, -23.09) * mm});
            skArc(sketch, "E124.trimOffspring", {"start": v(-24.76, -23.94) * mm, "mid": v(-24.36, -24.36) * mm, "end": v(-23.94, -24.76) * mm});
            skArc(sketch, "E125.trimOffspring", {"start": v(-23.09, -24.22) * mm, "mid": v(-22.9, -24.4) * mm, "end": v(-22.73, -24.56) * mm});
            skArc(sketch, "E126.trimOffspring", {"start": v(-23.21, -25.45) * mm, "mid": v(-22.78, -25.84) * mm, "end": v(-22.34, -26.22) * mm});
            skArc(sketch, "E127.trimOffspring", {"start": v(-21.52, -25.62) * mm, "mid": v(-21.33, -25.78) * mm, "end": v(-21.14, -25.94) * mm});
            skArc(sketch, "E128.trimOffspring", {"start": v(-21.57, -26.86) * mm, "mid": v(-21.11, -27.22) * mm, "end": v(-20.65, -27.57) * mm});
            skArc(sketch, "E129.trimOffspring", {"start": v(-19.87, -26.93) * mm, "mid": v(-19.67, -27.07) * mm, "end": v(-19.47, -27.22) * mm});
            skArc(sketch, "E130.trimOffspring", {"start": v(-18.14, -28.12) * mm, "mid": v(-17.93, -28.25) * mm, "end": v(-17.72, -28.39) * mm});
            skArc(sketch, "E131.trimOffspring", {"start": v(-18.03, -29.35) * mm, "mid": v(-17.53, -29.65) * mm, "end": v(-17.03, -29.94) * mm});
            skArc(sketch, "E132.trimOffspring", {"start": v(-16.34, -29.2) * mm, "mid": v(-16.12, -29.33) * mm, "end": v(-15.9, -29.44) * mm});
            skArc(sketch, "E133.trimOffspring", {"start": v(-16.15, -30.42) * mm, "mid": v(-15.64, -30.7) * mm, "end": v(-15.12, -30.95) * mm});
            skLineSegment(sketch, "E134", {"start": v(-19.84, -28.16) * mm, "end": v(-18.88, -28.81) * mm});
            skArc(sketch, "E135.trimOffspring", {"start": v(-14.47, -30.17) * mm, "mid": v(-14.25, -30.28) * mm, "end": v(-14.02, -30.39) * mm});
            skArc(sketch, "E136.trimOffspring", {"start": v(-14.21, -31.38) * mm, "mid": v(-13.68, -31.61) * mm, "end": v(-13.14, -31.84) * mm});
            skArc(sketch, "E137.trimOffspring", {"start": v(-12.55, -31.02) * mm, "mid": v(-12.32, -31.11) * mm, "end": v(-12.09, -31.2) * mm});
            skArc(sketch, "E138.trimOffspring", {"start": v(-12.21, -32.2) * mm, "mid": v(-11.67, -32.4) * mm, "end": v(-11.12, -32.6) * mm});
            skArc(sketch, "E139.trimOffspring", {"start": v(-10.17, -32.91) * mm, "mid": v(-9.6, -33.08) * mm, "end": v(-9.05, -33.23) * mm});
            skArc(sketch, "E140.trimOffspring", {"start": v(-8.56, -32.35) * mm, "mid": v(-8.32, -32.41) * mm, "end": v(-8.08, -32.47) * mm});
            skLineSegment(sketch, "E141", {"start": v(-10.58, -31.75) * mm, "end": v(-10.1, -31.9) * mm});
            skArc(sketch, "E142.trimOffspring", {"start": v(-8.08, -33.48) * mm, "mid": v(-7.51, -33.62) * mm, "end": v(-6.94, -33.74) * mm});
            skArc(sketch, "E143.trimOffspring", {"start": v(-6.52, -32.82) * mm, "mid": v(-6.27, -32.87) * mm, "end": v(-6.02, -32.92) * mm});
            skArc(sketch, "E144.trimOffspring", {"start": v(-5.96, -33.93) * mm, "mid": v(-5.39, -34.02) * mm, "end": v(-4.81, -34.1) * mm});
            skArc(sketch, "E145.trimOffspring", {"start": v(-4.44, -33.17) * mm, "mid": v(-4.2, -33.2) * mm, "end": v(-3.95, -33.23) * mm});
            skArc(sketch, "E146.trimOffspring", {"start": v(-3.82, -34.23) * mm, "mid": v(-3.24, -34.3) * mm, "end": v(-2.66, -34.34) * mm});
            skArc(sketch, "E147.trimOffspring", {"start": v(-1.66, -34.4) * mm, "mid": v(-1.08, -34.43) * mm, "end": v(-0.5, -34.44) * mm});
            skArc(sketch, "E148.trimOffspring", {"start": v(0.5, -34.44) * mm, "mid": v(1.08, -34.43) * mm, "end": v(1.66, -34.4) * mm});
            skArc(sketch, "E149.trimOffspring", {"start": v(-0.25, -33.46) * mm, "mid": v(0, -33.46) * mm, "end": v(0.25, -33.46) * mm});
            skLineSegment(sketch, "E150", {"start": v(-2.35, -33.38) * mm, "end": v(-1.85, -33.41) * mm});
            skArc(sketch, "E151.trimOffspring", {"start": v(1.85, -33.41) * mm, "mid": v(2.1, -33.4) * mm, "end": v(2.35, -33.38) * mm});
            skArc(sketch, "E152.trimOffspring", {"start": v(2.66, -34.34) * mm, "mid": v(3.24, -34.3) * mm, "end": v(3.82, -34.23) * mm});
            skArc(sketch, "E153.trimOffspring", {"start": v(3.95, -33.23) * mm, "mid": v(4.2, -33.2) * mm, "end": v(4.44, -33.17) * mm});
            skArc(sketch, "E154.trimOffspring", {"start": v(4.81, -34.1) * mm, "mid": v(5.39, -34.02) * mm, "end": v(5.96, -33.93) * mm});
            skArc(sketch, "E155.trimOffspring", {"start": v(6.02, -32.92) * mm, "mid": v(6.27, -32.87) * mm, "end": v(6.52, -32.82) * mm});
            skArc(sketch, "E156.trimOffspring", {"start": v(6.94, -33.74) * mm, "mid": v(7.51, -33.62) * mm, "end": v(8.08, -33.48) * mm});
            skArc(sketch, "E157.trimOffspring", {"start": v(8.08, -32.47) * mm, "mid": v(8.32, -32.41) * mm, "end": v(8.56, -32.35) * mm});
            skArc(sketch, "E158.trimOffspring", {"start": v(9.05, -33.23) * mm, "mid": v(9.6, -33.08) * mm, "end": v(10.17, -32.91) * mm});
            skArc(sketch, "E159.trimOffspring", {"start": v(10.1, -31.9) * mm, "mid": v(10.34, -31.83) * mm, "end": v(10.58, -31.75) * mm});
            skArc(sketch, "E160.trimOffspring", {"start": v(11.12, -32.6) * mm, "mid": v(11.67, -32.4) * mm, "end": v(12.21, -32.2) * mm});
            skArc(sketch, "E161.trimOffspring", {"start": v(12.09, -31.2) * mm, "mid": v(12.32, -31.11) * mm, "end": v(12.55, -31.02) * mm});
            skArc(sketch, "E162.trimOffspring", {"start": v(13.14, -31.84) * mm, "mid": v(13.68, -31.61) * mm, "end": v(14.21, -31.38) * mm});
            skArc(sketch, "E163.trimOffspring", {"start": v(14.02, -30.39) * mm, "mid": v(14.25, -30.28) * mm, "end": v(14.47, -30.17) * mm});
            skArc(sketch, "E164.trimOffspring", {"start": v(15.12, -30.95) * mm, "mid": v(15.64, -30.7) * mm, "end": v(16.15, -30.42) * mm});
            skArc(sketch, "E165.trimOffspring", {"start": v(15.9, -29.44) * mm, "mid": v(16.12, -29.33) * mm, "end": v(16.34, -29.2) * mm});
            skArc(sketch, "E166.trimOffspring", {"start": v(17.03, -29.94) * mm, "mid": v(17.53, -29.65) * mm, "end": v(18.03, -29.35) * mm});
            skArc(sketch, "E167.trimOffspring", {"start": v(17.72, -28.39) * mm, "mid": v(17.93, -28.25) * mm, "end": v(18.14, -28.12) * mm});
            skArc(sketch, "E168.trimOffspring", {"start": v(18.88, -28.81) * mm, "mid": v(19.36, -28.49) * mm, "end": v(19.84, -28.16) * mm});
            skArc(sketch, "E169.trimOffspring", {"start": v(19.47, -27.22) * mm, "mid": v(19.67, -27.07) * mm, "end": v(19.87, -26.93) * mm});
            skArc(sketch, "E170.trimOffspring", {"start": v(20.65, -27.57) * mm, "mid": v(21.11, -27.22) * mm, "end": v(21.57, -26.86) * mm});
            skArc(sketch, "E171.trimOffspring", {"start": v(21.14, -25.94) * mm, "mid": v(21.33, -25.78) * mm, "end": v(21.52, -25.62) * mm});
            skArc(sketch, "E172.trimOffspring", {"start": v(22.34, -26.22) * mm, "mid": v(22.78, -25.84) * mm, "end": v(23.21, -25.45) * mm});
            skArc(sketch, "E173.trimOffspring", {"start": v(22.73, -24.56) * mm, "mid": v(22.9, -24.4) * mm, "end": v(23.09, -24.22) * mm});
            skArc(sketch, "E174.trimOffspring", {"start": v(23.94, -24.76) * mm, "mid": v(24.36, -24.36) * mm, "end": v(24.76, -23.94) * mm});
            skArc(sketch, "E175.trimOffspring", {"start": v(24.22, -23.09) * mm, "mid": v(24.4, -22.9) * mm, "end": v(24.56, -22.73) * mm});
            skArc(sketch, "E176.trimOffspring", {"start": v(25.45, -23.21) * mm, "mid": v(25.84, -22.78) * mm, "end": v(26.22, -22.34) * mm});
            skArc(sketch, "E177.trimOffspring", {"start": v(25.62, -21.52) * mm, "mid": v(25.78, -21.33) * mm, "end": v(25.94, -21.14) * mm});
            skArc(sketch, "E178.trimOffspring", {"start": v(26.86, -21.57) * mm, "mid": v(27.22, -21.11) * mm, "end": v(27.57, -20.65) * mm});
            skArc(sketch, "E179.trimOffspring", {"start": v(26.93, -19.87) * mm, "mid": v(27.07, -19.67) * mm, "end": v(27.22, -19.47) * mm});
            skArc(sketch, "E180.trimOffspring", {"start": v(28.16, -19.84) * mm, "mid": v(28.49, -19.36) * mm, "end": v(28.81, -18.88) * mm});
            skArc(sketch, "E181.trimOffspring", {"start": v(28.12, -18.14) * mm, "mid": v(28.25, -17.93) * mm, "end": v(28.39, -17.72) * mm});
            skArc(sketch, "E182.trimOffspring", {"start": v(29.35, -18.03) * mm, "mid": v(29.65, -17.53) * mm, "end": v(29.94, -17.03) * mm});
            skArc(sketch, "E183.trimOffspring", {"start": v(29.2, -16.34) * mm, "mid": v(29.33, -16.12) * mm, "end": v(29.44, -15.9) * mm});
            skArc(sketch, "E184.trimOffspring", {"start": v(30.42, -16.15) * mm, "mid": v(30.7, -15.64) * mm, "end": v(30.95, -15.12) * mm});
            skArc(sketch, "E185.trimOffspring", {"start": v(30.17, -14.47) * mm, "mid": v(30.28, -14.25) * mm, "end": v(30.39, -14.02) * mm});
            skArc(sketch, "E186.trimOffspring", {"start": v(31.38, -14.21) * mm, "mid": v(31.61, -13.68) * mm, "end": v(31.84, -13.14) * mm});
            skArc(sketch, "E187.trimOffspring", {"start": v(31.02, -12.55) * mm, "mid": v(31.11, -12.32) * mm, "end": v(31.2, -12.09) * mm});
            skArc(sketch, "E188.trimOffspring", {"start": v(32.2, -12.21) * mm, "mid": v(32.4, -11.67) * mm, "end": v(32.6, -11.12) * mm});
            skArc(sketch, "E189.trimOffspring", {"start": v(31.75, -10.58) * mm, "mid": v(31.83, -10.34) * mm, "end": v(31.9, -10.1) * mm});
            skArc(sketch, "E190.trimOffspring", {"start": v(32.91, -10.17) * mm, "mid": v(33.08, -9.6) * mm, "end": v(33.23, -9.05) * mm});
            skArc(sketch, "E191.trimOffspring", {"start": v(32.35, -8.56) * mm, "mid": v(32.41, -8.32) * mm, "end": v(32.47, -8.08) * mm});
            skArc(sketch, "E192.trimOffspring", {"start": v(33.48, -8.08) * mm, "mid": v(33.62, -7.51) * mm, "end": v(33.74, -6.94) * mm});
            skArc(sketch, "E193.trimOffspring", {"start": v(32.82, -6.52) * mm, "mid": v(32.87, -6.27) * mm, "end": v(32.92, -6.02) * mm});
            skArc(sketch, "E194.trimOffspring", {"start": v(33.93, -5.96) * mm, "mid": v(34.02, -5.39) * mm, "end": v(34.1, -4.81) * mm});
            skArc(sketch, "E195.trimOffspring", {"start": v(33.17, -4.44) * mm, "mid": v(33.2, -4.2) * mm, "end": v(33.23, -3.95) * mm});
            skArc(sketch, "E196.trimOffspring", {"start": v(34.23, -3.82) * mm, "mid": v(34.3, -3.24) * mm, "end": v(34.34, -2.66) * mm});
            skArc(sketch, "E197.trimOffspring", {"start": v(33.38, -2.35) * mm, "mid": v(33.4, -2.1) * mm, "end": v(33.41, -1.85) * mm});
            skArc(sketch, "E198.trimOffspring", {"start": v(34.4, -1.66) * mm, "mid": v(34.43, -1.08) * mm, "end": v(34.44, -0.5) * mm});
            skLineSegment(sketch, "E199", {"start": v(-8.56, 32.35) * mm, "end": v(-8.08, 32.47) * mm});
            skLineSegment(sketch, "E200", {"start": v(12.09, 31.2) * mm, "end": v(12.55, 31.02) * mm});
            skLineSegment(sketch, "E201", {"start": v(17.72, 28.39) * mm, "end": v(18.14, 28.12) * mm});
            skLineSegment(sketch, "E202", {"start": v(19.47, 27.22) * mm, "end": v(19.87, 26.93) * mm});
            skLineSegment(sketch, "E203", {"start": v(29.2, 16.34) * mm, "end": v(29.44, 15.9) * mm});
            skSolve(sketch);
        }
        {
            var Q0;
            Q0=makeQuery(id+"F0.imprint","IMPRINT",FACE,{"disambiguationData":[TD([[makeQuery(id+"F0.imprint","IMPRINT",EDGE,{"derivedFrom":sQuery(id+"F0.wireOp",EDGE,"E0")}),1.0]])]});
            extrude(context, id + "F1", {"entities" : qUnion([Q0]), "depth" : 25.59 * mm});
        }
        {
            var Q0;
            Q0=makeQuery(id+"F1.opExtrude","SWEPT_EDGE",EDGE,{"disambiguationData":[OSD([sQuery(id+"F0.wireOp",EDGE,"E0"),sQuery(id+"F0.wireOp",EDGE,"E2")])]});
            cPlane(context, id + "F2", {"entities" : qUnion([Q0]), "cplaneType" : CPlaneType.LINE_ANGLE, "offset" : 0 * mm, "angle" : 90 * degree, "width" : 150 * mm, "height" : 150 * mm});
        }
    });
